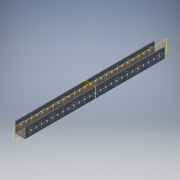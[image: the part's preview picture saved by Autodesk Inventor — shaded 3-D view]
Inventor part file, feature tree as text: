
AUTODESK INVENTOR PART (.ipt)
format: ipt  version: 2019 (Build 230136000, 136)  size: 633,344 bytes
history: native  units: in
note: dims shown in document units (in); Inventor stores cm internally (conversion verified against a paired STEP export)
features: other x216, plane x2, imported_body x1
ambient origin geometry x8: Origin, YZ Plane, XZ Plane, XY Plane, X Axis, Y Axis, Z Axis, Center Point
bodies: Body1 (feature_tree)
feature tree (219):
  other  "tetrix_739069_2012"
  other  "tetrix_739069_20121"
  other  "A_1"
  other  "A_78"
  other  "A_79"
  other  "A_80"
  other  "A_81"
  other  "A_82"
  other  "A_83"
  other  "A_84"
  other  "A_85"
  other  "A_27"
  other  "A_86"
  other  "A_87"
  other  "A_88"
  other  "A_89"
  other  "A_90"
  other  "A_91"
  other  "A_92"
  other  "A_93"
  other  "A_119"
  other  "A_120"
  other  "A_121"
  other  "A_122"
  other  "A_123"
  other  "A_124"
  other  "A_125"
  other  "A_126"
  other  "A_127"
  other  "A_149"
  other  "A_150"
  other  "A_151"
  other  "A_152"
  other  "A_153"
  other  "A_154"
  other  "A_155"
  other  "A_156"
  other  "A_157"
  other  "A_158"
  other  "A_159"
  other  "A_160"
  other  "A_161"
  other  "A_162"
  other  "A_163"
  other  "A_164"
  other  "A_165"
  other  "A_166"
  other  "Work Axis46"
  other  "Work Axis47"
  other  "Work Axis48"
  other  "Work Axis49"
  other  "Work Axis50"
  other  "Work Axis51"
  other  "Work Axis52"
  other  "Work Axis53"
  other  "Work Axis54"
  other  "Work Axis55"
  other  "Work Axis56"
  other  "Work Axis57"
  other  "Work Axis58"
  other  "Work Axis59"
  other  "Work Axis60"
  other  "Work Axis61"
  other  "Work Axis62"
  other  "Work Axis63"
  other  "A_18"
  other  "A_94"
  other  "A_95"
  other  "A_96"
  other  "A_97"
  other  "A_98"
  other  "A_99"
  other  "A_100"
  other  "A_101"
  other  "A_31"
  other  "A_102"
  other  "A_103"
  other  "A_104"
  other  "A_105"
  other  "A_106"
  other  "A_107"
  other  "A_108"
  other  "A_109"
  other  "A_128"
  other  "A_129"
  other  "A_130"
  other  "A_131"
  other  "A_132"
  other  "A_133"
  other  "A_134"
  other  "A_135"
  other  "A_136"
  other  "A_1283"
  other  "A_1284"
  other  "A_1285"
  other  "A_1286"
  other  "A_1287"
  other  "A_1288"
  other  "A_1289"
  other  "A_1290"
  other  "A_1291"
  other  "A_1292"
  other  "A_1293"
  other  "A_1294"
  other  "A_1295"
  other  "A_1296"
  other  "A_1297"
  other  "A_1298"
  other  "A_1299"
  other  "A_1300"
  other  "Work Axis109"
  other  "Work Axis110"
  other  "Work Axis111"
  other  "Work Axis112"
  other  "Work Axis113"
  other  "Work Axis114"
  other  "Work Axis115"
  other  "Work Axis116"
  other  "Work Axis117"
  other  "Work Axis118"
  other  "Work Axis119"
  other  "Work Axis120"
  other  "Work Axis121"
  other  "Work Axis122"
  other  "Work Axis123"
  other  "Work Axis124"
  other  "Work Axis125"
  other  "Work Axis126"
  other  "A_77"
  other  "A_110"
  other  "A_111"
  other  "A_112"
  other  "A_113"
  other  "A_139"
  other  "A_140"
  other  "A_141"
  other  "A_142"
  other  "A_143"
  other  "A_2421"
  other  "A_2422"
  other  "A_2423"
  other  "A_2424"
  other  "A_2425"
  other  "A_2426"
  other  "A_2427"
  other  "A_2428"
  other  "A_2429"
  other  "A_2430"
  other  "A_2449"
  other  "A_2450"
  other  "A_2451"
  other  "A_2452"
  other  "A_2453"
  other  "A_2454"
  other  "A_2455"
  other  "A_2456"
  other  "A_2457"
  other  "A_2458"
  other  "A_114"
  other  "A_115"
  other  "A_116"
  other  "A_117"
  other  "A_118"
  other  "A_144"
  other  "A_145"
  other  "A_146"
  other  "A_147"
  other  "A_148"
  other  "A_2431"
  other  "A_2432"
  other  "A_2433"
  other  "A_2434"
  other  "A_2435"
  other  "A_2436"
  other  "A_2437"
  other  "A_2438"
  other  "A_2439"
  other  "A_2440"
  other  "A_2459"
  other  "A_2460"
  other  "A_2461"
  other  "A_2462"
  other  "A_2463"
  other  "A_2464"
  other  "A_2465"
  other  "A_2466"
  other  "A_2467"
  other  "A_2468"
  other  "A_75"
  other  "A_76"
  other  "A_137"
  other  "A_138"
  other  "A_2441"
  other  "A_2442"
  other  "A_2443"
  other  "A_2444"
  other  "A_2469"
  other  "A_2470"
  other  "A_2471"
  other  "A_2472"
  other  "A_2417"
  other  "A_2418"
  other  "A_2419"
  other  "A_2420"
  other  "A_2445"
  other  "A_2446"
  other  "A_2447"
  other  "A_2448"
  other  "A_2473"
  other  "A_2474"
  other  "A_2475"
  other  "A_2476"
  other  "FRONT"
  other  "TOP"
  other  "RIGHT"
  other  "DTM1"
  plane  "Work Plane5"
  plane  "Work Plane6"
  imported_body  "Base1"
